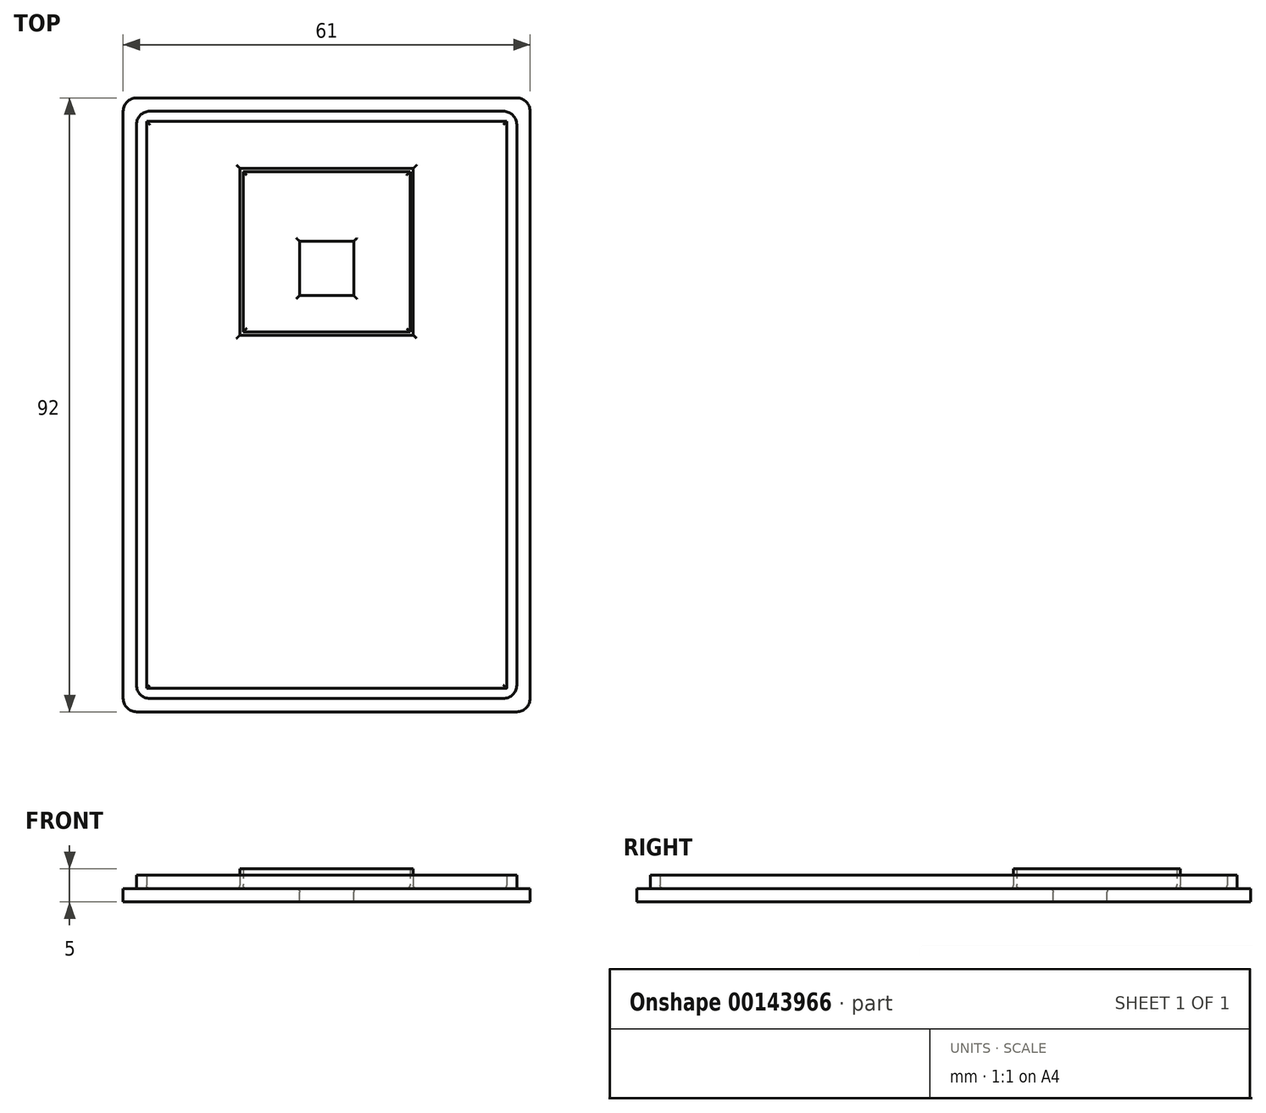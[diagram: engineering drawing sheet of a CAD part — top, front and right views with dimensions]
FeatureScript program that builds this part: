
annotation { "Feature Type Name" : "Feature", "Feature Type Description" : "" }
export const myFeature = defineFeature(function(context is Context, id is Id, definition is map)
    precondition{}
    {
        {
            var Q0;
            Q0=qCreatedBy(makeId("Top.planeOp"),FACE);
            var sketch = newSketch(context, id + "F0", { "sketchPlane" : qUnion([Q0])});
            skLineSegment(sketch, "E0", {"start": v(-28.5, 0) * mm, "end": v(-28.5, 42) * mm});
            skLineSegment(sketch, "E1", {"start": v(-26.5, 44) * mm, "end": v(26.5, 44) * mm});
            skLineSegment(sketch, "E2", {"start": v(28.5, 42) * mm, "end": v(28.5, 0) * mm});
            skLineSegment(sketch, "E3", {"start": v(28.5, 0) * mm, "end": v(28.5, -42) * mm});
            skLineSegment(sketch, "E4", {"start": v(26.5, -44) * mm, "end": v(-26.5, -44) * mm});
            skLineSegment(sketch, "E5", {"start": v(-28.5, -42) * mm, "end": v(-28.5, 0) * mm});
            skLineSegment(sketch, "E6", {"start": v(0, 0) * mm, "end": v(28.5, 0) * mm, "construction": true});
            skLineSegment(sketch, "E7", {"start": v(0, 0) * mm, "end": v(-28.5, 0) * mm, "construction": true});
            skPoint(sketch, "E8.visualSharp", {"position": v(-28.5, 44) * mm});
            skArc(sketch, "E8.filletArc", {"start": v(-26.5, 44) * mm, "mid": v(-27.91, 43.41) * mm, "end": v(-28.5, 42) * mm});
            skPoint(sketch, "E9.visualSharp", {"position": v(28.5, 44) * mm});
            skArc(sketch, "E9.filletArc", {"start": v(28.5, 42) * mm, "mid": v(27.91, 43.41) * mm, "end": v(26.5, 44) * mm});
            skPoint(sketch, "E10.visualSharp", {"position": v(28.5, -44) * mm});
            skArc(sketch, "E10.filletArc", {"start": v(26.5, -44) * mm, "mid": v(27.91, -43.41) * mm, "end": v(28.5, -42) * mm});
            skPoint(sketch, "E11.visualSharp", {"position": v(-28.5, -44) * mm});
            skArc(sketch, "E11.filletArc", {"start": v(-28.5, -42) * mm, "mid": v(-27.91, -43.41) * mm, "end": v(-26.5, -44) * mm});
            skLineSegment(sketch, "E12", {"start": v(-30.5, 0) * mm, "end": v(-30.5, 44) * mm});
            skLineSegment(sketch, "E13", {"start": v(-28.5, 46) * mm, "end": v(28.5, 46) * mm});
            skLineSegment(sketch, "E14", {"start": v(30.5, 44) * mm, "end": v(30.5, 0) * mm});
            skLineSegment(sketch, "E15", {"start": v(30.5, 0) * mm, "end": v(30.5, -44) * mm});
            skLineSegment(sketch, "E16", {"start": v(28.5, -46) * mm, "end": v(-28.5, -46) * mm});
            skLineSegment(sketch, "E17", {"start": v(-30.5, -44) * mm, "end": v(-30.5, 0) * mm});
            skPoint(sketch, "E18.visualSharp", {"position": v(-30.5, 46) * mm});
            skArc(sketch, "E18.filletArc", {"start": v(-28.5, 46) * mm, "mid": v(-29.91, 45.41) * mm, "end": v(-30.5, 44) * mm});
            skPoint(sketch, "E19.visualSharp", {"position": v(30.5, 46) * mm});
            skArc(sketch, "E19.filletArc", {"start": v(30.5, 44) * mm, "mid": v(29.91, 45.41) * mm, "end": v(28.5, 46) * mm});
            skPoint(sketch, "E20.visualSharp", {"position": v(30.5, -46) * mm});
            skArc(sketch, "E20.filletArc", {"start": v(28.5, -46) * mm, "mid": v(29.91, -45.41) * mm, "end": v(30.5, -44) * mm});
            skPoint(sketch, "E21.visualSharp", {"position": v(-30.5, -46) * mm});
            skArc(sketch, "E21.filletArc", {"start": v(-30.5, -44) * mm, "mid": v(-29.91, -45.41) * mm, "end": v(-28.5, -46) * mm});
            skLineSegment(sketch, "E22", {"start": v(0, 0) * mm, "end": v(0, -46) * mm, "construction": true});
            skPoint(sketch, "E23.cornerSnap0", {"position": v(-29.91, -45.41) * mm});
            skLineSegment(sketch, "E24.bottom", {"start": v(-27, 42.5) * mm, "end": v(27, 42.5) * mm});
            skLineSegment(sketch, "E24.top", {"start": v(-27, -42.5) * mm, "end": v(27, -42.5) * mm});
            skLineSegment(sketch, "E24.left", {"start": v(-27, 42.5) * mm, "end": v(-27, -42.5) * mm});
            skLineSegment(sketch, "E24.right", {"start": v(27, 42.5) * mm, "end": v(27, -42.5) * mm});
            skPoint(sketch, "E24.middle", {"position": v(0, 0) * mm});
            skLineSegment(sketch, "E25", {"start": v(0, 0) * mm, "end": v(0, 46) * mm, "construction": true});
            skSolve(sketch);
        }
        {
            var Q0;
            Q0=makeQuery(id+"F0.imprint","IMPRINT",FACE,{"disambiguationData":[TD([[makeQuery(id+"F0.imprint","IMPRINT",EDGE,{"derivedFrom":sQuery(id+"F0.wireOp",EDGE,"E0")}),1.0]])]});
            var Q1;
            Q1=makeQuery(id+"F0.imprint","IMPRINT",FACE,{"disambiguationData":[TD([[makeQuery(id+"F0.imprint","IMPRINT",EDGE,{"derivedFrom":sQuery(id+"F0.wireOp",EDGE,"E0")}),-1.0]])]});
            var Q2;
            Q2=makeQuery(id+"F0.imprint","IMPRINT",FACE,{"disambiguationData":[TD([[makeQuery(id+"F0.imprint","IMPRINT",EDGE,{"derivedFrom":sQuery(id+"F0.wireOp",EDGE,"E24.bottom")}),-1.0]])]});
            extrude(context, id + "F1", {"entities" : qUnion([Q0, Q1, Q2]), "oppositeDirection" : true, "depth" : 2 * mm});
        }
        {
            var Q0;
            Q0=makeQuery(id+"F0.imprint","IMPRINT",FACE,{"disambiguationData":[TD([[makeQuery(id+"F0.imprint","IMPRINT",EDGE,{"derivedFrom":sQuery(id+"F0.wireOp",EDGE,"E0")}),-1.0]])]});
            extrude(context, id + "F2", {"entities" : qUnion([Q0]), "operationType" : NewBodyOperationType.ADD, "depth" : 2 * mm});
        }
        {
            var Q0;
            Q0=qCreatedBy(makeId("Top.planeOp"),FACE);
            var sketch = newSketch(context, id + "F3", { "sketchPlane" : qUnion([Q0])});
            skLineSegment(sketch, "E26", {"start": v(-28.5, 0) * mm, "end": v(-28.5, 42) * mm});
            skLineSegment(sketch, "E27", {"start": v(-26.5, 44) * mm, "end": v(26.5, 44) * mm});
            skLineSegment(sketch, "E28", {"start": v(28.5, 42) * mm, "end": v(28.5, 0) * mm});
            skLineSegment(sketch, "E29", {"start": v(28.5, 0) * mm, "end": v(28.5, -42) * mm});
            skLineSegment(sketch, "E30", {"start": v(26.5, -44) * mm, "end": v(-26.5, -44) * mm});
            skLineSegment(sketch, "E31", {"start": v(-28.5, -42) * mm, "end": v(-28.5, 0) * mm});
            skLineSegment(sketch, "E32", {"start": v(0, 0) * mm, "end": v(28.5, 0) * mm, "construction": true});
            skLineSegment(sketch, "E33", {"start": v(0, 0) * mm, "end": v(-28.5, 0) * mm, "construction": true});
            skPoint(sketch, "E34.visualSharp", {"position": v(-28.5, 44) * mm});
            skArc(sketch, "E34.filletArc", {"start": v(-26.5, 44) * mm, "mid": v(-27.91, 43.41) * mm, "end": v(-28.5, 42) * mm});
            skPoint(sketch, "E35.visualSharp", {"position": v(28.5, 44) * mm});
            skArc(sketch, "E35.filletArc", {"start": v(28.5, 42) * mm, "mid": v(27.91, 43.41) * mm, "end": v(26.5, 44) * mm});
            skPoint(sketch, "E36.visualSharp", {"position": v(28.5, -44) * mm});
            skArc(sketch, "E36.filletArc", {"start": v(26.5, -44) * mm, "mid": v(27.91, -43.41) * mm, "end": v(28.5, -42) * mm});
            skPoint(sketch, "E37.visualSharp", {"position": v(-28.5, -44) * mm});
            skArc(sketch, "E37.filletArc", {"start": v(-28.5, -42) * mm, "mid": v(-27.91, -43.41) * mm, "end": v(-26.5, -44) * mm});
            skLineSegment(sketch, "E38", {"start": v(-30.5, 0) * mm, "end": v(-30.5, 44) * mm});
            skLineSegment(sketch, "E39", {"start": v(-28.5, 46) * mm, "end": v(28.5, 46) * mm});
            skLineSegment(sketch, "E40", {"start": v(30.5, 44) * mm, "end": v(30.5, 0) * mm});
            skLineSegment(sketch, "E41", {"start": v(30.5, 0) * mm, "end": v(30.5, -44) * mm});
            skLineSegment(sketch, "E42", {"start": v(28.5, -46) * mm, "end": v(-28.5, -46) * mm});
            skLineSegment(sketch, "E43", {"start": v(-30.5, -44) * mm, "end": v(-30.5, 0) * mm});
            skPoint(sketch, "E44.visualSharp", {"position": v(-30.5, 46) * mm});
            skArc(sketch, "E44.filletArc", {"start": v(-28.5, 46) * mm, "mid": v(-29.91, 45.41) * mm, "end": v(-30.5, 44) * mm});
            skPoint(sketch, "E45.visualSharp", {"position": v(30.5, 46) * mm});
            skArc(sketch, "E45.filletArc", {"start": v(30.5, 44) * mm, "mid": v(29.91, 45.41) * mm, "end": v(28.5, 46) * mm});
            skPoint(sketch, "E46.visualSharp", {"position": v(30.5, -46) * mm});
            skArc(sketch, "E46.filletArc", {"start": v(28.5, -46) * mm, "mid": v(29.91, -45.41) * mm, "end": v(30.5, -44) * mm});
            skPoint(sketch, "E47.visualSharp", {"position": v(-30.5, -46) * mm});
            skArc(sketch, "E47.filletArc", {"start": v(-30.5, -44) * mm, "mid": v(-29.91, -45.41) * mm, "end": v(-28.5, -46) * mm});
            skLineSegment(sketch, "E48", {"start": v(0, 0) * mm, "end": v(0, -46) * mm, "construction": true});
            skPoint(sketch, "E49.cornerSnap0", {"position": v(-29.91, -45.41) * mm});
            skLineSegment(sketch, "E50.bottom", {"start": v(-27, 42.5) * mm, "end": v(27, 42.5) * mm});
            skLineSegment(sketch, "E50.top", {"start": v(-27, -42.5) * mm, "end": v(27, -42.5) * mm});
            skLineSegment(sketch, "E50.left", {"start": v(-27, 42.5) * mm, "end": v(-27, -42.5) * mm});
            skLineSegment(sketch, "E50.right", {"start": v(27, 42.5) * mm, "end": v(27, -42.5) * mm});
            skPoint(sketch, "E50.middle", {"position": v(0, 0) * mm});
            skLineSegment(sketch, "E51", {"start": v(0, 0) * mm, "end": v(0, 46) * mm, "construction": true});
            skLineSegment(sketch, "E52.bottom", {"start": v(4.05, 16.4) * mm, "end": v(-4.05, 16.4) * mm});
            skLineSegment(sketch, "E52.top", {"start": v(4.05, 24.5) * mm, "end": v(-4.05, 24.5) * mm});
            skLineSegment(sketch, "E52.left", {"start": v(4.05, 16.4) * mm, "end": v(4.05, 24.5) * mm});
            skLineSegment(sketch, "E52.right", {"start": v(-4.05, 16.4) * mm, "end": v(-4.05, 24.5) * mm});
            skPoint(sketch, "E52.middle", {"position": v(0, 20.45) * mm});
            skLineSegment(sketch, "E53.bottom", {"start": v(-10.5, 20.45) * mm, "end": v(10.5, 20.45) * mm});
            skLineSegment(sketch, "E53.top", {"start": v(-10.5, 32.95) * mm, "end": v(10.5, 32.95) * mm});
            skLineSegment(sketch, "E53.left", {"start": v(-10.5, 20.45) * mm, "end": v(-10.5, 32.95) * mm});
            skLineSegment(sketch, "E53.right", {"start": v(10.5, 20.45) * mm, "end": v(10.5, 32.95) * mm});
            skPoint(sketch, "E53.middle", {"position": v(0, 26.7) * mm});
            skLineSegment(sketch, "E54.bottom", {"start": v(-12.5, 34.95) * mm, "end": v(12.5, 34.95) * mm});
            skLineSegment(sketch, "E54.top", {"start": v(-12.5, 10.95) * mm, "end": v(12.5, 10.95) * mm});
            skLineSegment(sketch, "E54.left", {"start": v(-12.5, 34.95) * mm, "end": v(-12.5, 10.95) * mm});
            skLineSegment(sketch, "E54.right", {"start": v(12.5, 34.95) * mm, "end": v(12.5, 10.95) * mm});
            skPoint(sketch, "E54.middle", {"position": v(0, 22.95) * mm});
            skLineSegment(sketch, "E55.bottom", {"start": v(-13, 35.45) * mm, "end": v(13, 35.45) * mm});
            skLineSegment(sketch, "E55.top", {"start": v(-13, 10.45) * mm, "end": v(13, 10.45) * mm});
            skLineSegment(sketch, "E55.left", {"start": v(-13, 35.45) * mm, "end": v(-13, 10.45) * mm});
            skLineSegment(sketch, "E55.right", {"start": v(13, 35.45) * mm, "end": v(13, 10.45) * mm});
            skSolve(sketch);
        }
        {
            var Q0;
            Q0=makeQuery(id+"F3.imprint","IMPRINT",FACE,{"disambiguationData":[TD([[makeQuery(id+"F3.imprint","IMPRINT",EDGE,{"derivedFrom":sQuery(id+"F3.wireOp",EDGE,"E54.bottom")}),1.0]])]});
            extrude(context, id + "F4", {"entities" : qUnion([Q0]), "operationType" : NewBodyOperationType.ADD, "depth" : 3 * mm});
        }
        {
            var Q0;
            {var subQ0=sQuery(id+"F3.wireOp",EDGE,"E52.bottom");Q0=makeQuery(id+"F3.imprint","IMPRINT",FACE,{"disambiguationData":[TD([[makeQuery(id+"F3.imprint","IMPRINT",EDGE,{"derivedFrom":subQ0}),-1.0]])]});}
            var Q1;
            {var subQ0=sQuery(id+"F3.wireOp",EDGE,"E52.top");Q1=makeQuery(id+"F3.imprint","IMPRINT",FACE,{"disambiguationData":[TD([[makeQuery(id+"F3.imprint","IMPRINT",EDGE,{"derivedFrom":subQ0}),1.0]])]});}
            extrude(context, id + "F5", {"entities" : qUnion([Q0, Q1]), "operationType" : NewBodyOperationType.REMOVE, "endBound" : BoundingType.UP_TO_NEXT, "oppositeDirection" : true, "depth" : 25 * mm});
        }
        {
            var Q0;
            Q0=makeQuery(id+"F4.boolean.opBoolean","SPLIT",FACE,{"disambiguationData":[TD([makeQuery(id+"F4.opExtrude","SWEPT_FACE",FACE,{"disambiguationData":[OSD([sQuery(id+"F3.wireOp",EDGE,"E54.bottom")])]})])],"derivedFrom":makeQuery(id+"F2.boolean.opBoolean","SPLIT",FACE,{"disambiguationData":[TD([makeQuery(id+"F2.opExtrude","SWEPT_FACE",FACE,{"disambiguationData":[OSD([sQuery(id+"F0.wireOp",EDGE,"E24.bottom")])]})])],"derivedFrom":makeQuery(id+"F1.opExtrude","CAP_FACE",FACE,{"disambiguationData":[OSD([sQuery(id+"F0.wireOp",EDGE,"E12"),sQuery(id+"F0.wireOp",EDGE,"E13"),sQuery(id+"F0.wireOp",EDGE,"E14"),sQuery(id+"F0.wireOp",EDGE,"E15"),sQuery(id+"F0.wireOp",EDGE,"E16"),sQuery(id+"F0.wireOp",EDGE,"E17"),sQuery(id+"F0.wireOp",EDGE,"E18.filletArc"),sQuery(id+"F0.wireOp",EDGE,"E19.filletArc"),sQuery(id+"F0.wireOp",EDGE,"E20.filletArc"),sQuery(id+"F0.wireOp",EDGE,"E21.filletArc")])],"isStart":true})})});
            var Q1;
            {var subQ3=makeQuery(id+"F2.opExtrude","SWEPT_FACE",FACE,{"disambiguationData":[OSD([sQuery(id+"F0.wireOp",EDGE,"E24.bottom")])]});Q1=makeQuery(id+"F4.boolean.opBoolean","SPLIT",FACE,{"disambiguationData":[TD([subQ3])],"derivedFrom":makeQuery(id+"F2.boolean.opBoolean","SPLIT",FACE,{"disambiguationData":[TD([subQ3])],"derivedFrom":makeQuery(id+"F1.opExtrude","CAP_FACE",FACE,{"disambiguationData":[OSD([sQuery(id+"F0.wireOp",EDGE,"E12"),sQuery(id+"F0.wireOp",EDGE,"E13"),sQuery(id+"F0.wireOp",EDGE,"E14"),sQuery(id+"F0.wireOp",EDGE,"E15"),sQuery(id+"F0.wireOp",EDGE,"E16"),sQuery(id+"F0.wireOp",EDGE,"E17"),sQuery(id+"F0.wireOp",EDGE,"E18.filletArc"),sQuery(id+"F0.wireOp",EDGE,"E19.filletArc"),sQuery(id+"F0.wireOp",EDGE,"E20.filletArc"),sQuery(id+"F0.wireOp",EDGE,"E21.filletArc")])],"isStart":true})})});}
            fillet(context, id + "F6", {"entities" : qUnion([Q0, Q1]), "radius" : .5 * mm, "tangentPropagation" : true, "allowEdgeOverflow" : false});
        }
    });
